# Revit family: GMi_Companies-M1_Whiteboards-1
name_source: partatom
category: Furniture
revit_build: Autodesk Revit 2014 (Build: 20130308_1515(x64)
units: mm (PartAtom-declared; Revit-internal decimal feet)

## types (4) — shared parameters
Assembly Code = E2020200
Board Finish = GMI - Porcelain
Depth = 3 1/32"
Frame Finish = GMI - Aluminum
Height = 24"
Keynote = 12500
Manufacturer = GMi Companies
Miscellaneous Finish = GMI - Plastic
Support Finish = GMI - Aluminum
Type Comments = Porcelain WB
URL = www.gmicompanies.com

## per-type parameters (varying)
| type | Description | Model | Width |
| MI-5x6 | M1 Porcelain magnetic whiteboard aluminum frame 5'H x 6'W | MI-5X6 | 72" |
| MI-5x8 | M1 Porcelain magnetic whiteboard aluminum frame 5'H x 8'W | MI-5x8 | 96" |
| MI-5x10 | M1 Porcelain magnetic whiteboard aluminum frame 5'H x 10'W | MI-5x10 | 120" |
| MI-5x12 | M1 Porcelain magnetic whiteboard aluminum frame 5'H x 12'W | MI-5x12 | 144" |

## geometry (parser evidence)
native form markers: Sweep x1
no freeform markers — native parametric forms only
